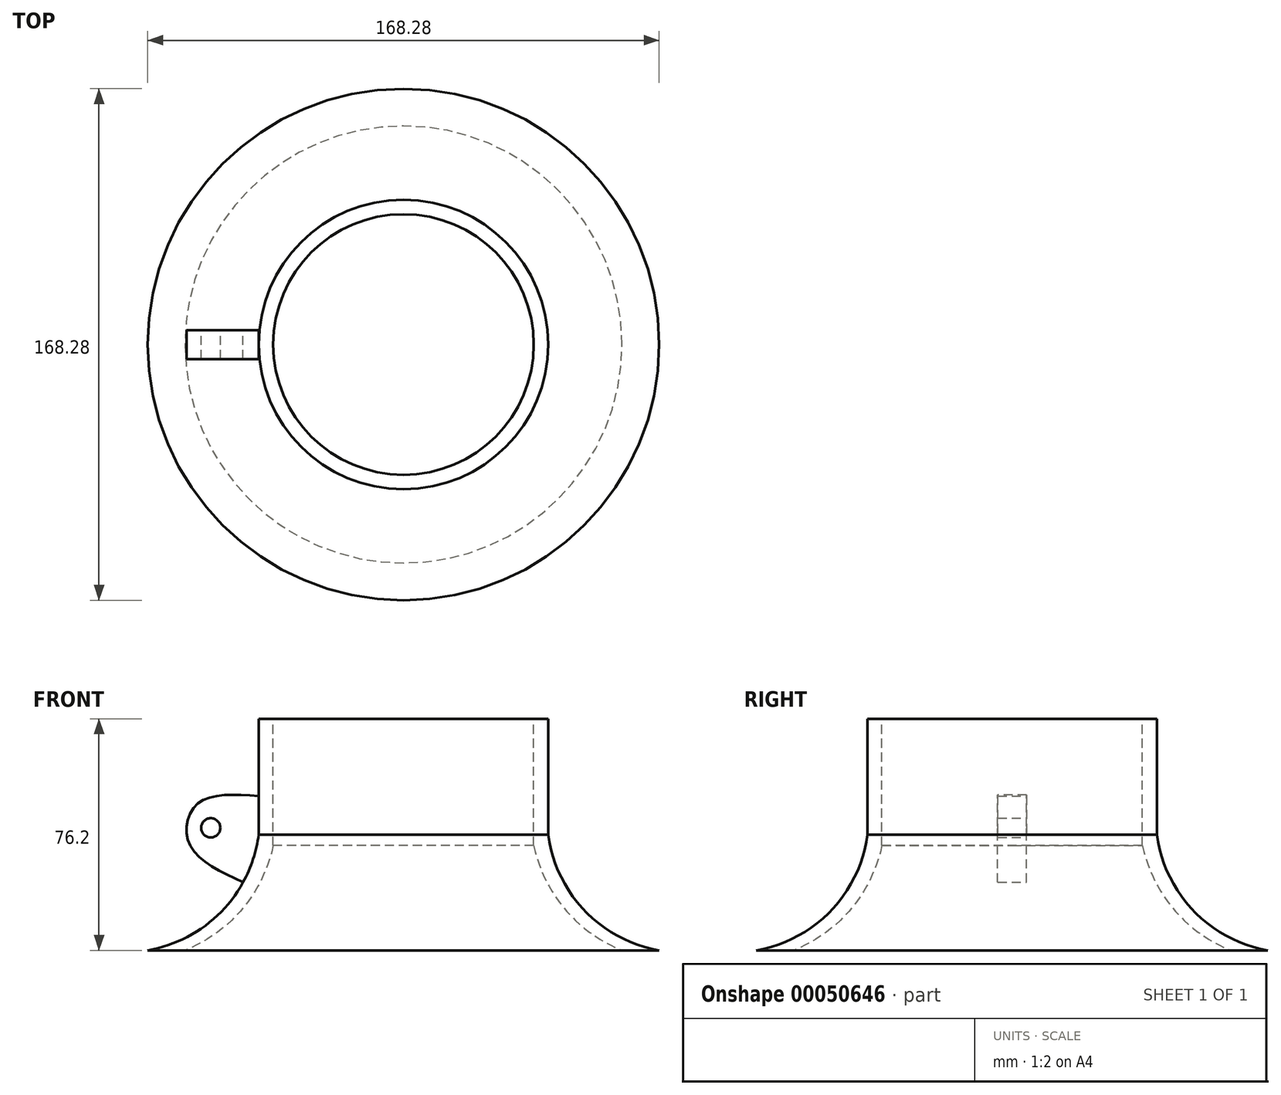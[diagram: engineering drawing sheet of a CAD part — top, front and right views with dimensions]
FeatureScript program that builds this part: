
annotation { "Feature Type Name" : "Feature", "Feature Type Description" : "" }
export const myFeature = defineFeature(function(context is Context, id is Id, definition is map)
    precondition{}
    {
        {
            var Q0;
            Q0=qCreatedBy(makeId("Front.planeOp"),FACE);
            var sketch = newSketch(context, id + "F0", { "sketchPlane" : qUnion([Q0])});
            skLineSegment(sketch, "E0", {"start": v(-47.63, 34.46) * mm, "end": v(-47.63, 76.2) * mm});
            skLineSegment(sketch, "E1", {"start": v(-47.63, 76.2) * mm, "end": v(-52.39, 76.2) * mm});
            skLineSegment(sketch, "E2", {"start": v(-52.39, 76.2) * mm, "end": v(-52.39, 38.1) * mm});
            skLineSegment(sketch, "E3", {"start": v(-82.5, 50.8) * mm, "end": v(8.32, 50.8) * mm, "construction": true});
            skArc(sketch, "E4", {"start": v(-88.9, 0) * mm, "mid": v(-64.39, 13.05) * mm, "end": v(-52.39, 38.1) * mm});
            skPoint(sketch, "E5.orphan", {"position": v(-52.39, 0) * mm});
            skPoint(sketch, "E6.orphan", {"position": v(-52.39, 38.1) * mm});
            skArc(sketch, "E7", {"start": v(-76.65, 0) * mm, "mid": v(-57.84, 13.6) * mm, "end": v(-47.62, 34.46) * mm});
            skLineSegment(sketch, "E8.trimOffspring", {"start": v(-76.65, 0) * mm, "end": v(-88.9, 0) * mm});
            skPoint(sketch, "E9.start.orphan", {"position": v(-47.63, 0) * mm});
            skFitSpline(sketch, "E10", {"points": [v(-57.53, 22.38) * mm, v(-75.2, 35.04) * mm, v(-72.56, 48.18) * mm, v(-52.39, 50.8) * mm], "startDerivative": vector(-62.4, 28.97) * mm, "endDerivative": vector(67.68, -4.47) * mm});
            skCircle(sketch, "E11", {"center": v(-68.18, 40.3) * mm, "radius": 3.18 * mm});
            skLineSegment(sketch, "E12", {"start": v(-4.76, 88.1) * mm, "end": v(-4.76, -17.75) * mm});
            skSolve(sketch);
        }
        {
            var Q0;
            Q0=makeQuery(id+"F0.imprint","IMPRINT",FACE,{"disambiguationData":[TD([[makeQuery(id+"F0.imprint","IMPRINT",EDGE,{"derivedFrom":sQuery(id+"F0.wireOp",EDGE,"E0")}),1.0]])]});
            var Q1;
            Q1=sQuery(id+"F0.wireOp",EDGE,"E12");
            revolve(context, id + "F1", {"entities" : qUnion([Q0]), "axis" : qUnion([Q1]), "revolveType" : RevolveType.FULL});
        }
        {
            var Q0;
            {var subQ3=sQuery(id+"F0.wireOp",EDGE,"E10");Q0=makeQuery(id+"F0.imprint","IMPRINT",FACE,{"disambiguationData":[TD([[makeQuery(id+"F0.imprint","IMPRINT",EDGE,{"derivedFrom":subQ3}),-1.0]])]});}
            extrude(context, id + "F2", {"entities" : qUnion([Q0]), "operationType" : NewBodyOperationType.ADD, "endBound" : BoundingType.SYMMETRIC, "depth" : 9.52 * mm});
        }
    });
